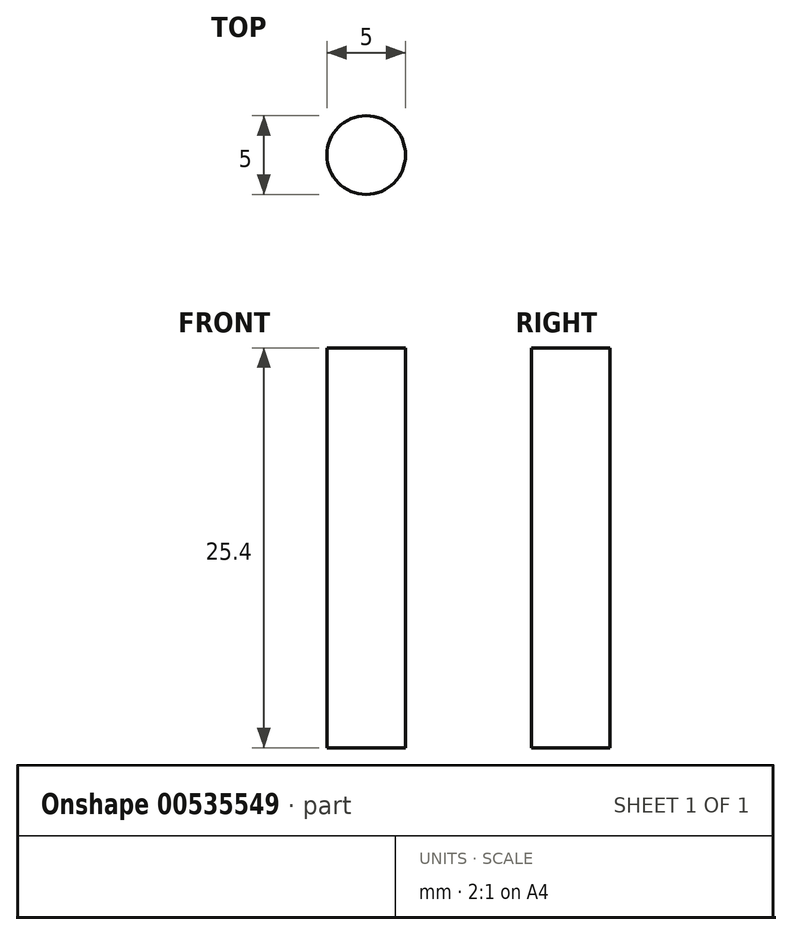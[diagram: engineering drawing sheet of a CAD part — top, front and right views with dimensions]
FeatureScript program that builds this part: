
annotation { "Feature Type Name" : "Feature", "Feature Type Description" : "" }
export const myFeature = defineFeature(function(context is Context, id is Id, definition is map)
    precondition{}
    {
        {
            var Q0;
            Q0=qCreatedBy(makeId("Top.planeOp"),FACE);
            var sketch = newSketch(context, id + "F0", { "sketchPlane" : qUnion([Q0])});
            skCircle(sketch, "E0", {"center": v(0, 0) * mm, "radius": 2.5 * mm});
            skSolve(sketch);
        }
        {
            var Q0;
            Q0 = qSketchRegion(id + "F0", true);
            extrude(context, id + "F1", {"entities" : qUnion([Q0]), "depth" : 25.4 * mm, "offsetDistance" : 25 * mm});
        }
    });
